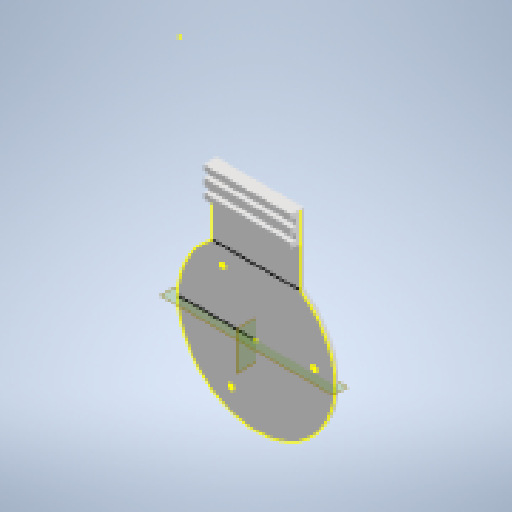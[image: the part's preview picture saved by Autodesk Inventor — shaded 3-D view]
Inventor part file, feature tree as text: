
AUTODESK INVENTOR PART (.ipt)
format: ipt  version: 2023 (Build 270158000, 158)  size: 531,456 bytes
history: native  units: mm
features: other x14, sketch x12, extrude x9, projected_geometry x3
ambient origin geometry x8: Origin, YZ Plane, XZ Plane, XY Plane, X Axis, Y Axis, Z Axis, Center Point
bodies: Solide1 (feature_tree)
feature tree (38):
  extrude  "Extrusion1"  Depth=0.5mm
  extrude  "Extrusion12"  Depth=50.0mm
  extrude  "Extrusion21"  Depth=3.0mm
  extrude  "Extrusion22"  Depth=3.0mm
  extrude  "Extrusion23"  Depth=2.9mm TaperAngle=0.0deg
  extrude  "Extrusion24"  Depth=2.0mm TaperAngle=0.0deg
  sketch  "Esquisse28"
  other  "Plan de construction5"
  other  "Plan de construction6"
  extrude  "Extrusion25"  Depth=5.0mm TaperAngle=0.0deg
  extrude  "Extrusion26"  Depth=15.0mm TaperAngle=0.0deg
  sketch  "Esquisse31"
  extrude  "Extrusion29"  Depth=90.0mm
  sketch  "Esquisse35"
  sketch  "Esquisse1"
  other  "Référence1"
  other  "Référence2"
  sketch  "Esquisse13"
  sketch  "Esquisse24"
  sketch  "Esquisse25"
  sketch  "Esquisse26"
  sketch  "Esquisse27"
  projected_geometry  "Boucle projetée10"
  sketch  "Esquisse29"
  other  "Référence3"
  other  "Référence4"
  other  "Référence5"
  sketch  "Esquisse30"
  projected_geometry  "Boucle projetée11"
  other  "Référence6"
  other  "Référence7"
  sketch  "Esquisse34"
  projected_geometry  "Boucle projetée12"
  other  "<userpath>\Desktop\PE-SM\3D\Ensemble.iam"
  other  "Ensemble.iam"
  other  "PE:1"
  other  "Ensemble1"
  other  "Anemometre-v1:1"
